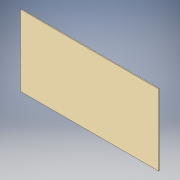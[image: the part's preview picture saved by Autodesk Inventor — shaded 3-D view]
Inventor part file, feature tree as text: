
AUTODESK INVENTOR PART (.ipt)
format: ipt  version: 2019 (Build 230136000, 136)  size: 89,088 bytes
history: native  units: mm
features: extrude x1, sketch x1
ambient origin geometry x8: Origin, YZ Plane, XZ Plane, XY Plane, X Axis, Y Axis, Z Axis, Center Point
bodies: Solid1 (feature_tree)
feature tree (2):
  extrude  "Extrusion1"  Depth=774.7mm
  sketch  "Sketch1"  dims[d0=4.7625mm d1=0.0mm d2=774.7mm d3=398.78mm]
